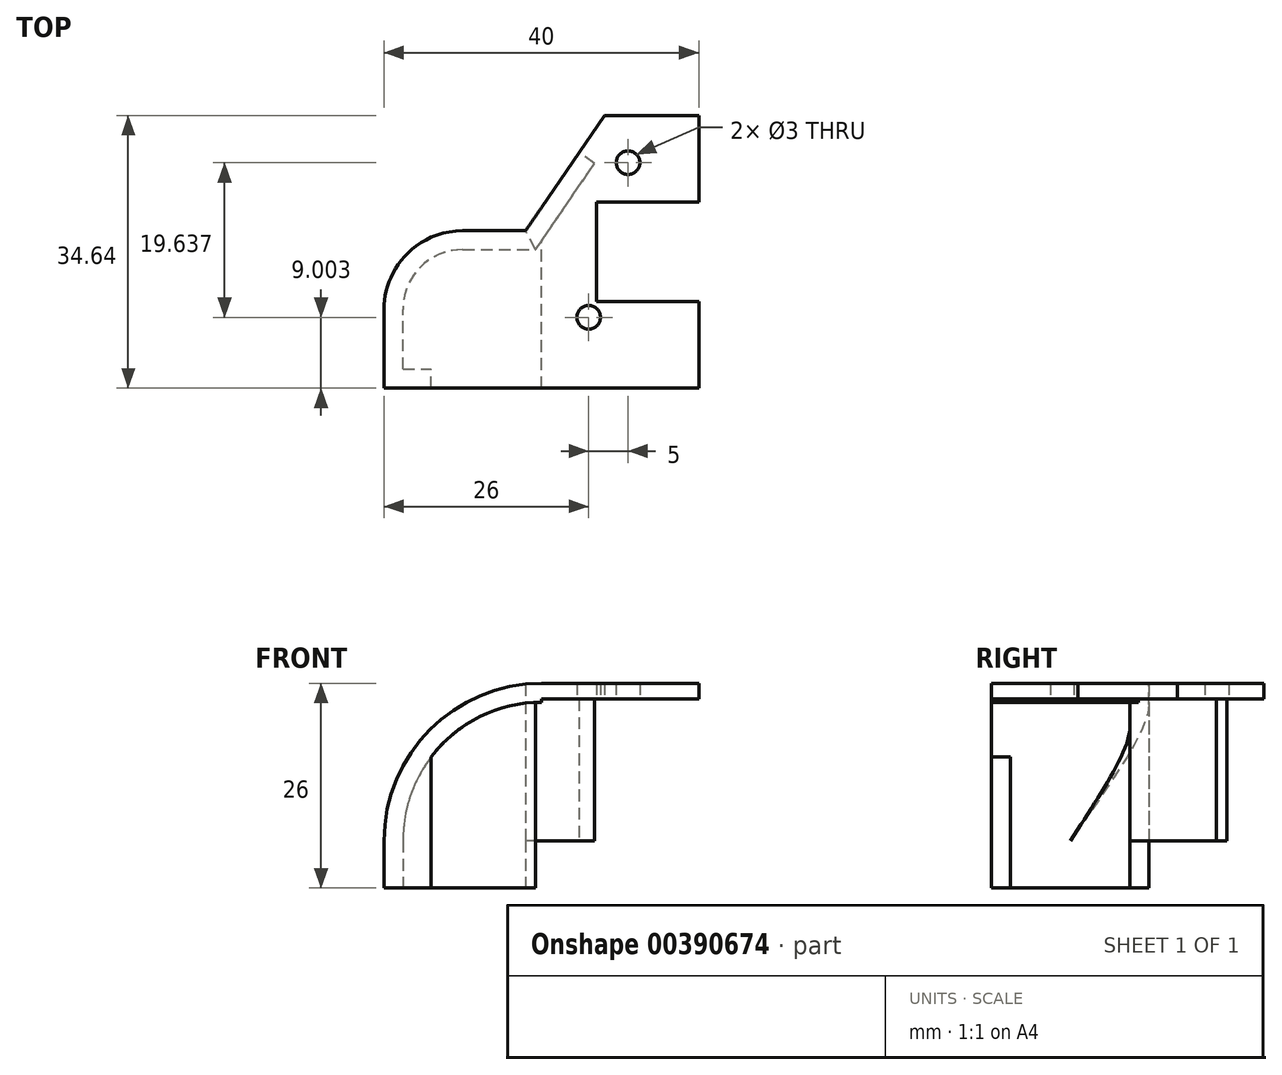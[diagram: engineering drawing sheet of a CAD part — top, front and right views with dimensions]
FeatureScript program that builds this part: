
annotation { "Feature Type Name" : "Feature", "Feature Type Description" : "" }
export const myFeature = defineFeature(function(context is Context, id is Id, definition is map)
    precondition{}
    {
        {
            var Q0;
            Q0=qCreatedBy(makeId("Top.planeOp"),FACE);
            var sketch = newSketch(context, id + "F0", { "sketchPlane" : qUnion([Q0])});
            skLineSegment(sketch, "E0", {"start": v(20, -17.64) * mm, "end": v(-20, -17.64) * mm});
            skLineSegment(sketch, "E1", {"start": v(-20, -17.64) * mm, "end": v(-20, -7.64) * mm});
            skLineSegment(sketch, "E2", {"start": v(-10, 2.36) * mm, "end": v(-2, 2.36) * mm});
            skLineSegment(sketch, "E3", {"start": v(20, 17) * mm, "end": v(8, 17) * mm});
            skLineSegment(sketch, "E4", {"start": v(8, 17) * mm, "end": v(-2, 2.36) * mm});
            skLineSegment(sketch, "E5", {"start": v(20, 17) * mm, "end": v(20, 6) * mm});
            skLineSegment(sketch, "E6", {"start": v(20, 6) * mm, "end": v(7, 6) * mm});
            skPoint(sketch, "E7.endSnap0", {"position": v(-20, -7.64) * mm});
            skLineSegment(sketch, "E8", {"start": v(20, -17.64) * mm, "end": v(20, -6.64) * mm});
            skLineSegment(sketch, "E9", {"start": v(7, 6) * mm, "end": v(7, -6.64) * mm});
            skLineSegment(sketch, "E10", {"start": v(7, -6.64) * mm, "end": v(20, -6.64) * mm});
            skCircle(sketch, "E11", {"center": v(11, 11) * mm, "radius": 1.5 * mm});
            skCircle(sketch, "E12", {"center": v(6, -8.64) * mm, "radius": 1.5 * mm});
            skPoint(sketch, "E13.visualSharp", {"position": v(-20, 2.36) * mm});
            skLineSegment(sketch, "E13.filletArc", {"start": v(-20, 2.36) * mm, "end": v(-20, 2.36) * mm});
            skArc(sketch, "E14.filletArc", {"start": v(-10, 2.36) * mm, "mid": v(-17.07, -0.57) * mm, "end": v(-20, -7.64) * mm});
            skSolve(sketch);
        }
        {
            var Q0;
            Q0 = qSketchRegion(id + "F0", true);
            extrude(context, id + "F1", {"entities" : qUnion([Q0]), "depth" : 2 * mm, "offsetDistance" : 25 * mm});
        }
        {
            var Q0;
            Q0=makeQuery(id+"F1.opExtrude","CAP_FACE",FACE,{"disambiguationData":[OSD([sQuery(id+"F0.wireOp",EDGE,"E0"),sQuery(id+"F0.wireOp",EDGE,"E1"),sQuery(id+"F0.wireOp",EDGE,"E2"),sQuery(id+"F0.wireOp",EDGE,"E3"),sQuery(id+"F0.wireOp",EDGE,"E4"),sQuery(id+"F0.wireOp",EDGE,"E5"),sQuery(id+"F0.wireOp",EDGE,"E6"),sQuery(id+"F0.wireOp",EDGE,"E8"),sQuery(id+"F0.wireOp",EDGE,"E9"),sQuery(id+"F0.wireOp",EDGE,"E10"),sQuery(id+"F0.wireOp",EDGE,"E11"),sQuery(id+"F0.wireOp",EDGE,"E12"),sQuery(id+"F0.wireOp",EDGE,"E13.filletArc")])],"isStart":true});
            extrude(context, id + "F2", {"entities" : qUnion([Q0]), "operationType" : NewBodyOperationType.ADD, "depth" : 24 * mm, "offsetDistance" : 25 * mm});
        }
        {
            var Q0;
            {var subQ0=sQuery(id+"F0.wireOp",EDGE,"E0");Q0=makeQuery(id+"F2.boolean.opBoolean","MERGE",FACE,{"derivedFrom":[makeQuery(id+"F1.opExtrude","SWEPT_FACE",FACE,{"disambiguationData":[OSD([subQ0])]}),makeQuery(id+"F2.opExtrude","SWEPT_FACE",FACE,{"disambiguationData":[OSD([subQ0])]})]});}
            var sketch = newSketch(context, id + "F3", { "sketchPlane" : qUnion([Q0])});
            skLineSegment(sketch, "E15", {"start": v(-20, -18) * mm, "end": v(-20, -11) * mm});
            skLineSegment(sketch, "E16", {"start": v(-7, 2) * mm, "end": v(0, 2) * mm});
            skPoint(sketch, "E17.visualSharp", {"position": v(-20, 2) * mm});
            skArc(sketch, "E17.filletArc", {"start": v(0, 2) * mm, "mid": v(-14.14, -3.86) * mm, "end": v(-20, -18) * mm});
            skSolve(sketch);
        }
        {
            var Q0;
            Q0 = qSketchRegion(id + "F3", true);
            var Q1;
            {var subQ6=sQuery(id+"F3.wireOp",EDGE,"E15");Q1=makeQuery(id+"F3.imprint","IMPRINT",FACE,{"disambiguationData":[TD([[makeQuery(id+"F3.imprint","IMPRINT",EDGE,{"derivedFrom":subQ6}),1.0]])]});}
            extrude(context, id + "F4", {"entities" : qUnion([Q0, Q1]), "operationType" : NewBodyOperationType.REMOVE, "oppositeDirection" : true, "depth" : 25 * mm, "offsetDistance" : 25 * mm});
        }
        {
            var Q0;
            Q0=makeQuery(id+"F2.opExtrude","CAP_FACE",FACE,{"disambiguationData":[OSD([sQuery(id+"F0.wireOp",EDGE,"E0"),sQuery(id+"F0.wireOp",EDGE,"E1"),sQuery(id+"F0.wireOp",EDGE,"E2"),sQuery(id+"F0.wireOp",EDGE,"E3"),sQuery(id+"F0.wireOp",EDGE,"E4"),sQuery(id+"F0.wireOp",EDGE,"E5"),sQuery(id+"F0.wireOp",EDGE,"E6"),sQuery(id+"F0.wireOp",EDGE,"E8"),sQuery(id+"F0.wireOp",EDGE,"E9"),sQuery(id+"F0.wireOp",EDGE,"E10"),sQuery(id+"F0.wireOp",EDGE,"E11"),sQuery(id+"F0.wireOp",EDGE,"E12"),sQuery(id+"F0.wireOp",EDGE,"E13.filletArc")])],"isStart":false});
            var sketch = newSketch(context, id + "F5", { "sketchPlane" : qUnion([Q0])});
            skLineSegment(sketch, "E18", {"start": v(-20, 17.64) * mm, "end": v(-14, 17.64) * mm});
            skLineSegment(sketch, "E19", {"start": v(-2, -2.36) * mm, "end": v(4.77, -12.27) * mm});
            skLineSegment(sketch, "E20", {"start": v(6.75, -10.92) * mm, "end": v(4.77, -12.27) * mm});
            skLineSegment(sketch, "E21.0", {"start": v(-17.6, 15.24) * mm, "end": v(-14, 15.24) * mm});
            skLineSegment(sketch, "E21.1", {"start": v(-0.73, 0.04) * mm, "end": v(6.75, -10.92) * mm});
            skLineSegment(sketch, "E21.2", {"start": v(-10, 0.04) * mm, "end": v(-0.73, 0.04) * mm});
            skArc(sketch, "E21.3", {"start": v(-10, 0.04) * mm, "mid": v(-15.37, 2.26) * mm, "end": v(-17.6, 7.64) * mm});
            skLineSegment(sketch, "E21.4", {"start": v(-17.6, 15.24) * mm, "end": v(-17.6, 7.64) * mm});
            skLineSegment(sketch, "E22", {"start": v(-14, 17.64) * mm, "end": v(-14, 15.24) * mm});
            skLineSegment(sketch, "E23", {"start": v(-0.73, 0.04) * mm, "end": v(-2, -2.36) * mm});
            skSolve(sketch);
        }
        {
            var Q0;
            Q0=makeQuery(id+"F5.imprint","IMPRINT",FACE,{"disambiguationData":[TD([[makeQuery(id+"F5.imprint","IMPRINT",EDGE,{"derivedFrom":sQuery(id+"F5.wireOp",EDGE,"4a108b7f-645f-4e34-8225-f8d35106aefd.0")}),-1.0]])]});
            var Q1;
            {var subQ5=sQuery(id+"F5.wireOp",EDGE,"E20");Q1=makeQuery(id+"F5.imprint","IMPRINT",FACE,{"disambiguationData":[TD([[makeQuery(id+"F5.imprint","IMPRINT",EDGE,{"derivedFrom":subQ5}),1.0]])]});}
            extrude(context, id + "F6", {"entities" : qUnion([Q0, Q1]), "operationType" : NewBodyOperationType.REMOVE, "oppositeDirection" : true, "depth" : 24 * mm, "offsetDistance" : 25 * mm});
        }
        {
            var Q0;
            {var subQ0=sQuery(id+"F0.wireOp",EDGE,"E1");var subQ1=sQuery(id+"F0.wireOp",EDGE,"E0");Q0=makeQuery(id+"F6.boolean.opBoolean","SPLIT",FACE,{"disambiguationData":[TD([makeQuery(id+"F1.opExtrude","SWEPT_FACE",FACE,{"disambiguationData":[OSD([subQ0])]})])],"derivedFrom":makeQuery(id+"F2.boolean.opBoolean","MERGE",FACE,{"derivedFrom":[makeQuery(id+"F1.opExtrude","SWEPT_FACE",FACE,{"disambiguationData":[OSD([subQ1])]}),makeQuery(id+"F2.opExtrude","SWEPT_FACE",FACE,{"disambiguationData":[OSD([subQ1])]})]})});}
            var sketch = newSketch(context, id + "F7", { "sketchPlane" : qUnion([Q0])});
            skLineSegment(sketch, "E24", {"start": v(-20, -18) * mm, "end": v(-20, -18) * mm});
            skLineSegment(sketch, "E25", {"start": v(0, 2) * mm, "end": v(0, 2) * mm});
            skPoint(sketch, "E26.visualSharp", {"position": v(-20, 2) * mm});
            skArc(sketch, "E26.filletArc", {"start": v(0, 2) * mm, "mid": v(-14.14, -3.86) * mm, "end": v(-20, -18) * mm});
            skArc(sketch, "E27.0", {"start": v(0, -0.4) * mm, "mid": v(-12.45, -5.55) * mm, "end": v(-17.6, -18) * mm});
            skLineSegment(sketch, "E28", {"start": v(-20, -18) * mm, "end": v(-17.6, -18) * mm});
            skLineSegment(sketch, "E29", {"start": v(0, 2) * mm, "end": v(0, -0.4) * mm});
            skSolve(sketch);
        }
        {
            var Q0;
            Q0 = qSketchRegion(id + "F7", true);
            extrude(context, id + "F8", {"entities" : qUnion([Q0]), "operationType" : NewBodyOperationType.ADD, "oppositeDirection" : true, "depth" : 20 * mm, "offsetDistance" : 25 * mm});
        }
        {
            var Q0;
            Q0=makeQuery(id+"F5.imprint","IMPRINT",FACE,{"disambiguationData":[TD([[makeQuery(id+"F5.imprint","IMPRINT",EDGE,{"derivedFrom":sQuery(id+"F5.wireOp",EDGE,"E18")}),1.0]])]});
            var sketch = newSketch(context, id + "F9", { "sketchPlane" : qUnion([Q0])});
            skArc(sketch, "E30.0", {"start": v(-10, -7.36) * mm, "mid": v(-20.6, -2.97) * mm, "end": v(-25, 7.64) * mm});
            skLineSegment(sketch, "E31", {"start": v(-25, 7.64) * mm, "end": v(-20, 7.64) * mm});
            skLineSegment(sketch, "E32", {"start": v(-10, -7.36) * mm, "end": v(-10, -2.36) * mm});
            skArc(sketch, "E33.0", {"start": v(-10, -2.36) * mm, "mid": v(-17.07, 0.57) * mm, "end": v(-20, 7.64) * mm});
            skSolve(sketch);
        }
        {
            var Q0;
            Q0 = qSketchRegion(id + "F9", true);
            extrude(context, id + "F10", {"entities" : qUnion([Q0]), "operationType" : NewBodyOperationType.REMOVE, "oppositeDirection" : true, "depth" : 25 * mm, "offsetDistance" : 25 * mm});
        }
        {
            var Q0;
            Q0=makeQuery(id+"F5.imprint","IMPRINT",FACE,{"disambiguationData":[TD([[makeQuery(id+"F5.imprint","IMPRINT",EDGE,{"derivedFrom":sQuery(id+"F5.wireOp",EDGE,"E19")}),-1.0]])]});
            extrude(context, id + "F11", {"entities" : qUnion([Q0]), "operationType" : NewBodyOperationType.REMOVE, "oppositeDirection" : true, "depth" : 6 * mm, "offsetDistance" : 25 * mm});
        }
    });
